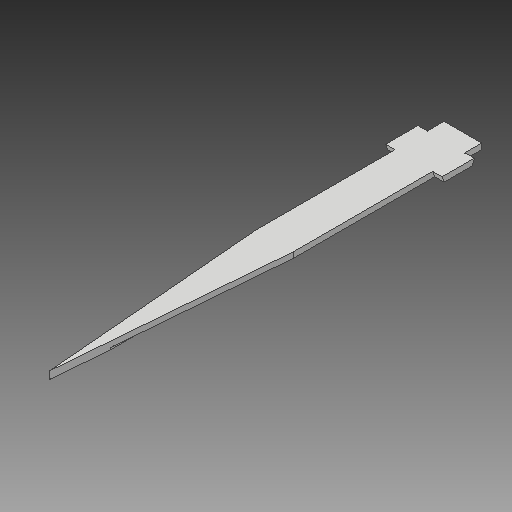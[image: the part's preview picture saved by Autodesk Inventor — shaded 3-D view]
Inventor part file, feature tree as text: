
AUTODESK INVENTOR PART (.ipt)
format: ipt  version: 2017 (Build 210142000, 142)  size: 122,368 bytes
history: native  units: mm
features: draft x4, extrude x2, sketch x2
ambient origin geometry x8: Origin, YZ Plane, XZ Plane, XY Plane, X Axis, Y Axis, Z Axis, Center Point
bodies: Solid1 (feature_tree)
feature tree (8):
  extrude  "Cuerpo"  Depth=20.0mm
  extrude  "Rail"  Depth=1.0mm
  draft  "FaceDraft1"
  draft  "FaceDraft2"
  draft  "FaceDraft3"
  draft  "FaceDraft4"
  sketch  "Sketch1"  dims[d0=100.0mm d1=20.0mm]
  sketch  "Sketch2"  dims[d2=220.0mm d3=10.0mm d4=15.0mm d5=5.0mm d6=10.0mm d7=3.0mm d8=0.0mm d9=5.0mm d10=1.0mm d11=0.0mm d12=-3.490659mm d13=-3.490659mm d14=-3.490659mm d15=-3.490659mm]
